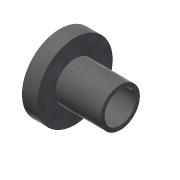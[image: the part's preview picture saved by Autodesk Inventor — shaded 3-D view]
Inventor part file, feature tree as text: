
AUTODESK INVENTOR PART (.ipt)
format: ipt  version: 2016 SP2 (Build 200236200, 236)  size: 101,888 bytes
history: native  units: mm
features: revolve x1, sketch x1
ambient origin geometry x8: Origin, YZ Plane, XZ Plane, XY Plane, X Axis, Y Axis, Z Axis, Center Point
bodies: Solid1 (feature_tree)
feature tree (2):
  revolve  "Revolution1"  [1 undecoded]
  sketch  "Sketch1"  dims[d0=3.75mm d1=1.55mm d2=1.95mm d3=6.0mm d4=4.5mm d5=90.0deg]
note: 1 required parameter value undecoded (feature->parameter linkage not recoverable at this tier; creation-order binding heuristic only, values carry confidence <= 0.55)
